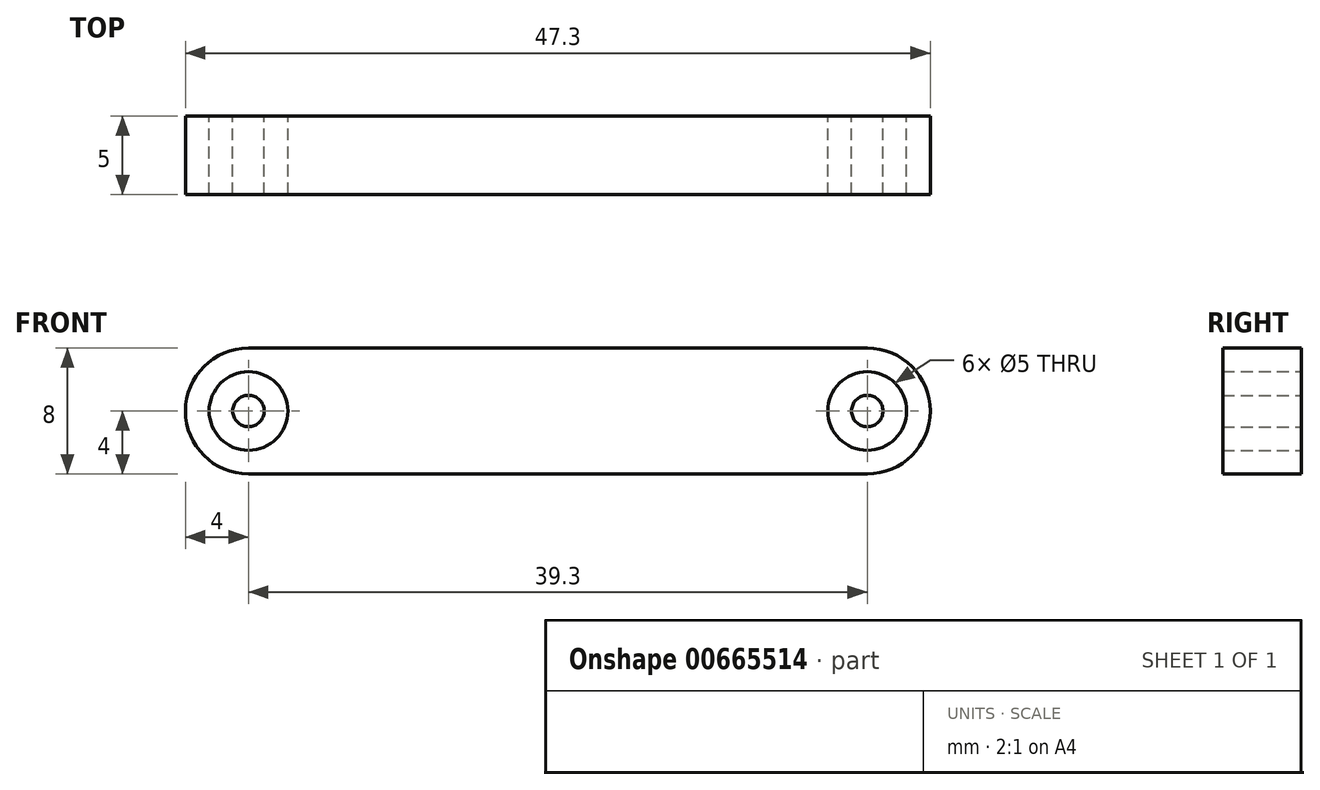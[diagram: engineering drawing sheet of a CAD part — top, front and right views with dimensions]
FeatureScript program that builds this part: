
annotation { "Feature Type Name" : "Feature", "Feature Type Description" : "" }
export const myFeature = defineFeature(function(context is Context, id is Id, definition is map)
    precondition{}
    {
        {
            var Q0;
            Q0=qCreatedBy(makeId("Front.planeOp"),FACE);
            var sketch = newSketch(context, id + "F0", { "sketchPlane" : qUnion([Q0])});
            skArc(sketch, "E0", {"start": v(0, 4) * mm, "mid": v(-4, 0) * mm, "end": v(0, -4) * mm});
            skArc(sketch, "E1", {"start": v(39.3, -4) * mm, "mid": v(43.3, 0) * mm, "end": v(39.3, 4) * mm});
            skLineSegment(sketch, "E2", {"start": v(0, 4) * mm, "end": v(39.3, 4) * mm});
            skLineSegment(sketch, "E3", {"start": v(0, -4) * mm, "end": v(39.3, -4) * mm});
            skCircle(sketch, "E4", {"center": v(0, 0) * mm, "radius": 2.5 * mm});
            skCircle(sketch, "E5", {"center": v(39.3, 0) * mm, "radius": 2.5 * mm});
            skCircle(sketch, "E6", {"center": v(0, 0) * mm, "radius": 1 * mm});
            skCircle(sketch, "E7", {"center": v(39.3, 0) * mm, "radius": 1 * mm});
            skSolve(sketch);
        }
        {
            var Q0;
            Q0 = qSketchRegion(id + "F0", true);
            var Q1;
            Q1=makeQuery(id+"F0.imprint","IMPRINT",FACE,{"disambiguationData":[TD([[makeQuery(id+"F0.imprint","IMPRINT",EDGE,{"derivedFrom":sQuery(id+"F0.wireOp",EDGE,"E6")}),1.0]])]});
            var Q2;
            Q2=makeQuery(id+"F0.imprint","IMPRINT",FACE,{"disambiguationData":[TD([[makeQuery(id+"F0.imprint","IMPRINT",EDGE,{"derivedFrom":sQuery(id+"F0.wireOp",EDGE,"E7")}),1.0]])]});
            extrude(context, id + "F1", {"entities" : qUnion([Q0, Q1, Q2]), "depth" : 5 * mm, "offsetDistance" : 25 * mm});
        }
    });
